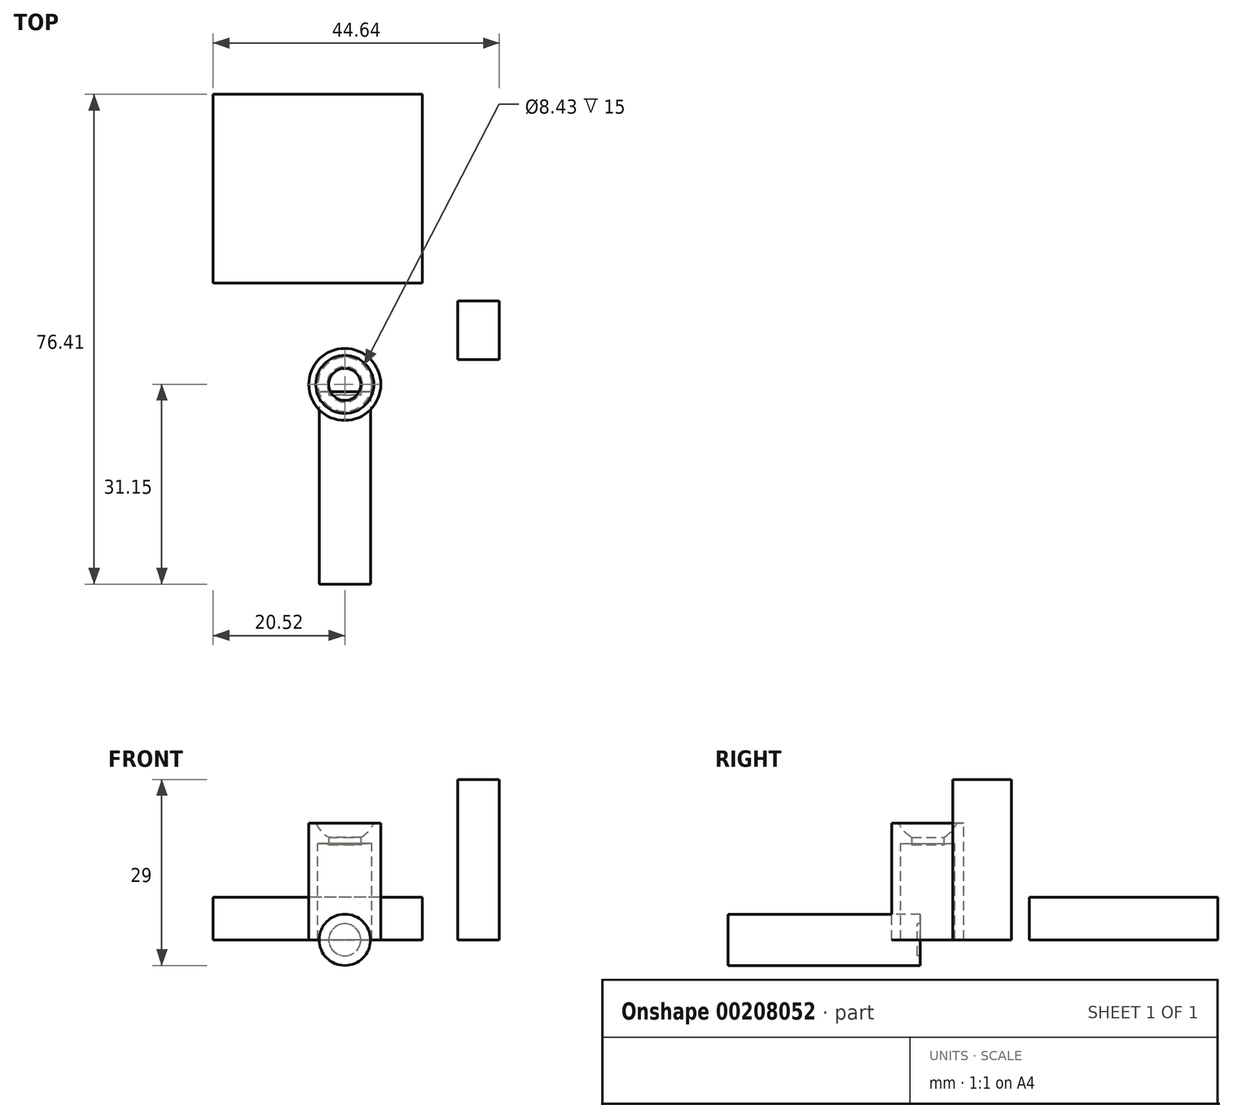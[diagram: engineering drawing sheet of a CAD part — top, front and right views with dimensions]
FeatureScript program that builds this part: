
annotation { "Feature Type Name" : "Feature", "Feature Type Description" : "" }
export const myFeature = defineFeature(function(context is Context, id is Id, definition is map)
    precondition{}
    {
        {
            var Q0;
            Q0=qCreatedBy(makeId("Top.planeOp"),FACE);
            var sketch = newSketch(context, id + "F0", { "sketchPlane" : qUnion([Q0])});
            skArc(sketch, "E0", {"start": v(0, 0) * mm, "mid": v(5, 5) * mm, "end": v(0, 10) * mm});
            skLineSegment(sketch, "E1", {"start": v(0, 10) * mm, "end": v(0, 0) * mm, "construction": true});
            skSolve(sketch);
        }
        {
            var Q0;
            Q0=sQuery(id+"F0.wireOp",EDGE,"E0");
            var Q1;
            Q1=sQuery(id+"F0.wireOp",EDGE,"E1");
            revolve(context, id + "F1", {"bodyType" : ToolBodyType.SURFACE, "surfaceEntities" : qUnion([Q0]), "axis" : qUnion([Q1]), "revolveType" : RevolveType.FULL});
        }
        {
            var Q0;
            Q0=qCreatedBy(makeId("Top.planeOp"),FACE);
            var sketch = newSketch(context, id + "F2", { "sketchPlane" : qUnion([Q0])});
            skLineSegment(sketch, "E2.bottom", {"start": v(-4, -0.5) * mm, "end": v(4, -0.5) * mm});
            skLineSegment(sketch, "E2.top", {"start": v(-4, -30.5) * mm, "end": v(4, -30.5) * mm});
            skLineSegment(sketch, "E2.left", {"start": v(-4, -0.5) * mm, "end": v(-4, -30.5) * mm});
            skLineSegment(sketch, "E2.right", {"start": v(4, -0.5) * mm, "end": v(4, -30.5) * mm});
            skLineSegment(sketch, "E3", {"start": v(0, -30.5) * mm, "end": v(0, -0.5) * mm});
            skLineSegment(sketch, "E4", {"start": v(0, 0) * mm, "end": v(0, -0.5) * mm, "construction": true});
            skSolve(sketch);
        }
        {
            var Q0;
            {var subQ0=sQuery(id+"F2.wireOp",EDGE,"E2.left");Q0=makeQuery(id+"F2.imprint","IMPRINT",FACE,{"disambiguationData":[TD([[makeQuery(id+"F2.imprint","IMPRINT",EDGE,{"derivedFrom":subQ0}),1.0]])]});}
            var Q1;
            Q1 = qSketchRegion(id + "F4", true);
            var Q2;
            Q2=sQuery(id+"F2.wireOp",EDGE,"E3");
            revolve(context, id + "F3", {"entities" : qUnion([Q0, Q1]), "axis" : qUnion([Q2]), "revolveType" : RevolveType.FULL});
        }
        {
            var Q0;
            Q0=qCreatedBy(makeId("Top.planeOp"),FACE);
            var sketch = newSketch(context, id + "F4", { "sketchPlane" : qUnion([Q0])});
            skArc(sketch, "E5", {"start": v(-4.53, 2.89) * mm, "mid": v(0, 0) * mm, "end": v(4.53, 2.89) * mm});
            skLineSegment(sketch, "E6", {"start": v(0, 5) * mm, "end": v(0, 0) * mm, "construction": true});
            skLineSegment(sketch, "E7", {"start": v(0, 5) * mm, "end": v(-4.53, 2.89) * mm, "construction": true});
            skLineSegment(sketch, "E8", {"start": v(0, 5) * mm, "end": v(4.53, 2.89) * mm, "construction": true});
            skArc(sketch, "E9.0", {"start": v(-2.78, -0.32) * mm, "mid": v(1.93, -0.68) * mm, "end": v(5.44, 2.46) * mm});
            skLineSegment(sketch, "E10", {"start": v(-4.53, 2.89) * mm, "end": v(-5.62, 2.89) * mm});
            skLineSegment(sketch, "E11", {"start": v(4.53, 2.89) * mm, "end": v(5.44, 2.46) * mm});
            skLineSegment(sketch, "E12", {"start": v(0, 0) * mm, "end": v(0, -1) * mm});
            skLineSegment(sketch, "E13", {"start": v(-4.22, -0.32) * mm, "end": v(-4.22, -15.32) * mm});
            skLineSegment(sketch, "E14", {"start": v(-4.22, -15.32) * mm, "end": v(-5.62, -15.32) * mm});
            skLineSegment(sketch, "E15", {"start": v(-5.62, -15.32) * mm, "end": v(-5.62, 2.89) * mm});
            skLineSegment(sketch, "E16.MirrorCS", {"start": v(4.22, 0.73) * mm, "end": v(4.22, -15.32) * mm});
            skLineSegment(sketch, "E17.MirrorCS", {"start": v(4.22, -15.32) * mm, "end": v(5.62, -15.32) * mm});
            skLineSegment(sketch, "E18.MirrorCS", {"start": v(5.62, -15.32) * mm, "end": v(5.62, 2.89) * mm});
            skLineSegment(sketch, "E19", {"start": v(-4.22, -0.32) * mm, "end": v(-2.78, -0.32) * mm});
            skLineSegment(sketch, "E20", {"start": v(-4.22, 0.73) * mm, "end": v(0, 0.73) * mm, "construction": true});
            skLineSegment(sketch, "E21", {"start": v(-4.22, 0.73) * mm, "end": v(-4.22, -0.32) * mm, "construction": true});
            skSolve(sketch);
        }
        {
            var Q0;
            {var subQ3=sQuery(id+"F4.wireOp",EDGE,"E10");Q0=makeQuery(id+"F4.imprint","IMPRINT",FACE,{"disambiguationData":[TD([[makeQuery(id+"F4.imprint","IMPRINT",EDGE,{"derivedFrom":subQ3}),1.0]])]});}
            var Q1;
            Q1=sQuery(id+"F4.wireOp",EDGE,"E12");
            revolve(context, id + "F5", {"entities" : qUnion([Q0]), "axis" : qUnion([Q1]), "revolveType" : RevolveType.FULL});
        }
        {
            var Q0;
            Q0=qCreatedBy(makeId("Front.planeOp"),FACE);
            var Q1;
            Q1 = qBodyType(qCreatedBy(id + "F7" ,EDGE), BodyType.WIRE);
            cPlane(context, id + "F6", {"entities" : qUnion([Q0, Q1]), "cplaneType" : CPlaneType.OFFSET, "offset" : 1 * mm, "width" : 150 * mm, "height" : 150 * mm});
        }
        {
            var Q0;
            Q0=qCreatedBy(id+"F6.planeOp",FACE);
            var sketch = newSketch(context, id + "F7", { "sketchPlane" : qUnion([Q0])});
            skCircle(sketch, "E22", {"center": v(0, 0) * mm, "radius": 2.5 * mm});
            skLineSegment(sketch, "E23", {"start": v(0, 0) * mm, "end": v(-2.5, 0) * mm, "construction": true});
            skSolve(sketch);
        }
        {
            var Q0;
            Q0 = qSketchRegion(id + "F7", true);
            extrude(context, id + "F8", {"entities" : qUnion([Q0]), "operationType" : NewBodyOperationType.REMOVE, "oppositeDirection" : true, "depth" : 25 * mm});
        }
        {
            var Q0;
            Q0=qCreatedBy(makeId("Top.planeOp"),FACE);
            var sketch = newSketch(context, id + "F9", { "sketchPlane" : qUnion([Q0])});
            skLineSegment(sketch, "E24.bottom", {"start": v(17.59, 13.7) * mm, "end": v(24.12, 13.7) * mm});
            skLineSegment(sketch, "E24.top", {"start": v(17.59, 4.55) * mm, "end": v(24.12, 4.55) * mm});
            skLineSegment(sketch, "E24.left", {"start": v(17.59, 13.7) * mm, "end": v(17.59, 4.55) * mm});
            skLineSegment(sketch, "E24.right", {"start": v(24.12, 13.7) * mm, "end": v(24.12, 4.55) * mm});
            skSolve(sketch);
        }
        {
            var Q0;
            Q0 = qSketchRegion(id + "F9", true);
            extrude(context, id + "F10", {"entities" : qUnion([Q0]), "depth" : 25 * mm});
        }
        {
            var Q0;
            Q0=makeQuery(id+"F5.opRevolve","SWEPT_BODY",BODY,{"disambiguationData":[OSD([sQuery(id+"F4.wireOp",EDGE,"E5"),sQuery(id+"F4.wireOp",EDGE,"E9.0"),sQuery(id+"F4.wireOp",EDGE,"E10"),sQuery(id+"F4.wireOp",EDGE,"E12"),sQuery(id+"F4.wireOp",EDGE,"E13"),sQuery(id+"F4.wireOp",EDGE,"E14"),sQuery(id+"F4.wireOp",EDGE,"E15"),sQuery(id+"F4.wireOp",EDGE,"E19")])]});
            var Q1;
            Q1=makeQuery(id+"F10.opExtrude","CAP_EDGE",EDGE,{"disambiguationData":[OSD([sQuery(id+"F9.wireOp",EDGE,"E24.top")])],"isStart":false});
            transform(context, id + "F11", {"entities" : qUnion([Q0]), "transformType" : TransformType.ROTATION, "transformAxis" : qUnion([Q1]), "angle" : 90 * degree, "makeCopy" : false});
        }
        {
            var Q0;
            Q0=makeQuery(id+"F5.opRevolve","SWEPT_BODY",BODY,{"disambiguationData":[OSD([sQuery(id+"F4.wireOp",EDGE,"E5"),sQuery(id+"F4.wireOp",EDGE,"E9.0"),sQuery(id+"F4.wireOp",EDGE,"E10"),sQuery(id+"F4.wireOp",EDGE,"E12"),sQuery(id+"F4.wireOp",EDGE,"E13"),sQuery(id+"F4.wireOp",EDGE,"E14"),sQuery(id+"F4.wireOp",EDGE,"E15"),sQuery(id+"F4.wireOp",EDGE,"E19")])]});
            var Q1;
            Q1=makeQuery(id+"F10.opExtrude","SWEPT_EDGE",EDGE,{"disambiguationData":[OSD([sQuery(id+"F9.wireOp",EDGE,"E24.bottom"),sQuery(id+"F9.wireOp",EDGE,"E24.left")])]});
            transform(context, id + "F12", {"entities" : qUnion([Q0]), "transformType" : TransformType.TRANSLATION_DISTANCE, "transformDirection" : qUnion([Q1]), "distance" : 1.5 * mm, "oppositeDirection" : true, "makeCopy" : false});
        }
        {
            var Q0;
            Q0=qCreatedBy(makeId("Top.planeOp"),FACE);
            var sketch = newSketch(context, id + "F13", { "sketchPlane" : qUnion([Q0])});
            skLineSegment(sketch, "E25.bottom", {"start": v(12.1, 16.46) * mm, "end": v(-20.52, 16.46) * mm});
            skLineSegment(sketch, "E25.top", {"start": v(12.1, 45.91) * mm, "end": v(-20.52, 45.91) * mm});
            skLineSegment(sketch, "E25.left", {"start": v(12.1, 16.46) * mm, "end": v(12.1, 45.91) * mm});
            skLineSegment(sketch, "E25.right", {"start": v(-20.52, 16.46) * mm, "end": v(-20.52, 45.91) * mm});
            skSolve(sketch);
        }
        {
            var Q0;
            Q0 = qSketchRegion(id + "F13", true);
            var Q1;
            Q1=makeQuery(id+"F5.opRevolve","SWEPT_FACE",FACE,{"disambiguationData":[OSD([sQuery(id+"F4.wireOp",EDGE,"E14")])]});
            extrude(context, id + "F14", {"entities" : qUnion([Q0]), "endBound" : BoundingType.UP_TO_SURFACE, "endBoundEntityFace" : qUnion([Q1]), "depth" : 25 * mm});
        }
        {
            var Q0;
            Q0=makeQuery(id+"F5.opRevolve","SWEPT_BODY",BODY,{"disambiguationData":[OSD([sQuery(id+"F4.wireOp",EDGE,"E5"),sQuery(id+"F4.wireOp",EDGE,"E9.0"),sQuery(id+"F4.wireOp",EDGE,"E10"),sQuery(id+"F4.wireOp",EDGE,"E12"),sQuery(id+"F4.wireOp",EDGE,"E13"),sQuery(id+"F4.wireOp",EDGE,"E14"),sQuery(id+"F4.wireOp",EDGE,"E15"),sQuery(id+"F4.wireOp",EDGE,"E19")])]});
            var Q1;
            Q1=makeQuery(id+"F14.opExtrude","SWEPT_EDGE",EDGE,{"disambiguationData":[OSD([sQuery(id+"F13.wireOp",EDGE,"E25.top"),sQuery(id+"F13.wireOp",EDGE,"E25.left")])]});
            transform(context, id + "F15", {"entities" : qUnion([Q0]), "transformType" : TransformType.TRANSLATION_ENTITY, "oppositeDirectionEntity" : false, "transformLine" : qUnion([Q1]), "makeCopy" : false});
        }
        {
            var Q0;
            Q0=makeQuery(id+"F5.opRevolve","SWEPT_BODY",BODY,{"disambiguationData":[OSD([sQuery(id+"F4.wireOp",EDGE,"E5"),sQuery(id+"F4.wireOp",EDGE,"E9.0"),sQuery(id+"F4.wireOp",EDGE,"E10"),sQuery(id+"F4.wireOp",EDGE,"E12"),sQuery(id+"F4.wireOp",EDGE,"E13"),sQuery(id+"F4.wireOp",EDGE,"E14"),sQuery(id+"F4.wireOp",EDGE,"E15"),sQuery(id+"F4.wireOp",EDGE,"E19")])]});
            transform(context, id + "F16", {"entities" : qUnion([Q0]), "transformType" : TransformType.TRANSLATION_3D, "dx" : 0 * mm, "dy" : -28.9 * mm, "dz" : 0 * mm, "makeCopy" : false});
        }
    });
